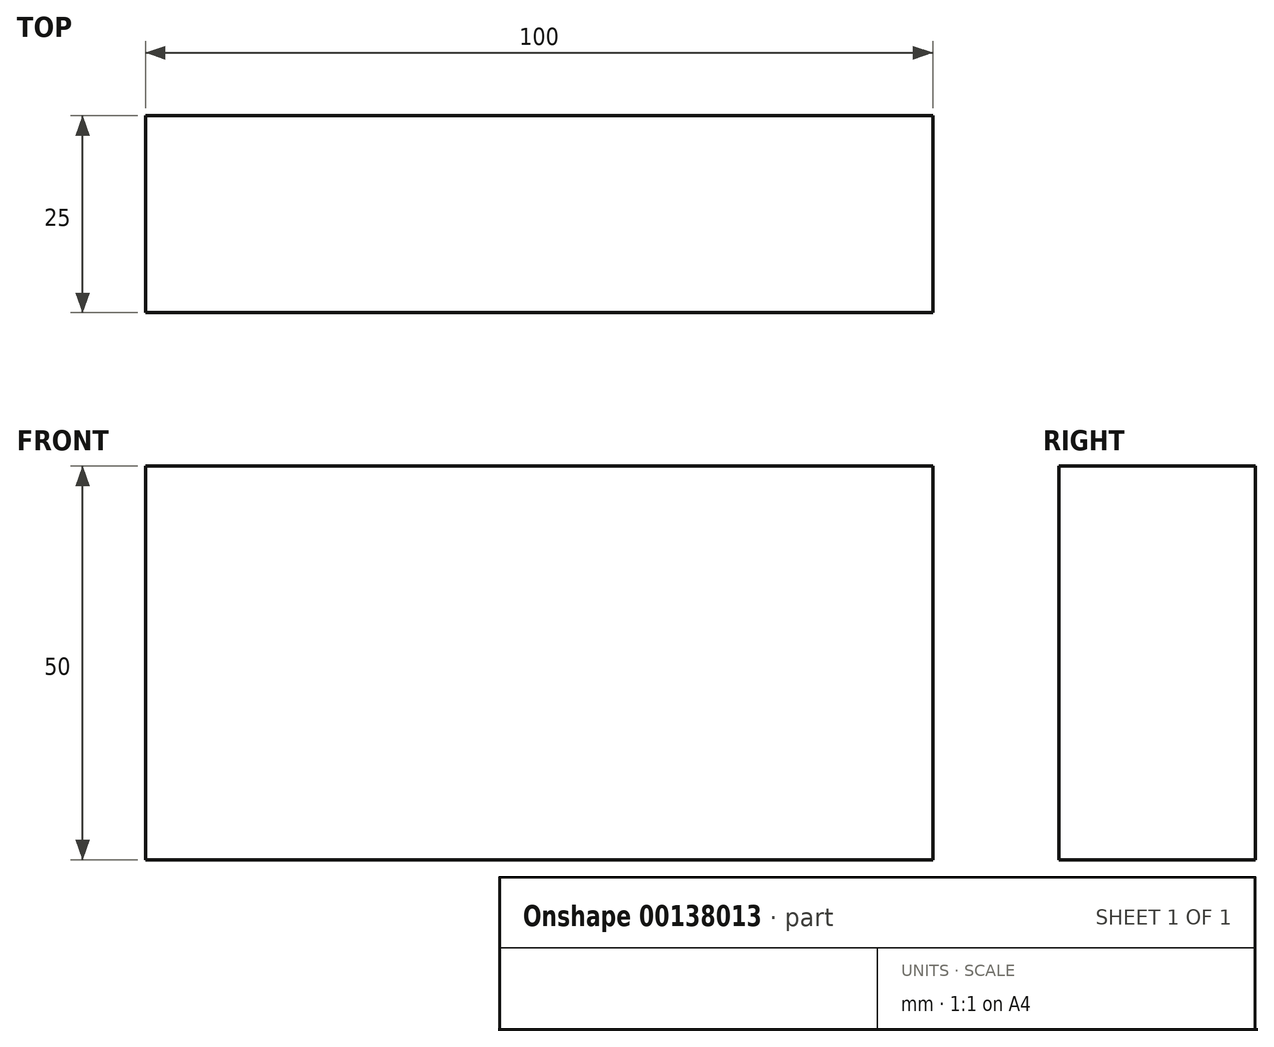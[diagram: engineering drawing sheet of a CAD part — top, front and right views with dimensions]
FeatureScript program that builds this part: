
annotation { "Feature Type Name" : "Feature", "Feature Type Description" : "" }
export const myFeature = defineFeature(function(context is Context, id is Id, definition is map)
    precondition{}
    {
        {
            var Q0;
            Q0=qCreatedBy(makeId("Front.planeOp"),FACE);
            var sketch = newSketch(context, id + "F0", { "sketchPlane" : qUnion([Q0])});
            skLineSegment(sketch, "E0", {"start": v(-36.86, -4.12) * mm, "end": v(-36.86, -54.12) * mm});
            skLineSegment(sketch, "E1", {"start": v(-36.86, -54.12) * mm, "end": v(63.14, -54.12) * mm});
            skLineSegment(sketch, "E2", {"start": v(-36.86, -4.12) * mm, "end": v(63.14, -4.12) * mm});
            skLineSegment(sketch, "E3", {"start": v(63.14, -4.12) * mm, "end": v(63.14, -54.12) * mm});
            skSolve(sketch);
        }
        {
            var Q0;
            Q0=makeQuery(id+"F0.imprint","IMPRINT",FACE,{"disambiguationData":[TD([[makeQuery(id+"F0.imprint","IMPRINT",EDGE,{"derivedFrom":sQuery(id+"F0.wireOp",EDGE,"E0")}),1.0]])]});
            extrude(context, id + "F1", {"entities" : qUnion([Q0]), "depth" : 25 * mm});
        }
    });
